# Revit family: Basin-Vanity_Sink-American_Standard-Studio_S-129700X
name_source: partatom
category: Plumbing Fixtures
units: mm (PartAtom-declared; Revit-internal decimal feet)

## family parameters
Always vertical = No
Cut with Voids When Loaded = Yes
OmniClass Number = 23.45.05.14.14
OmniClass Title = Sinks/Lavatories
Part Type = Normal
Room Calculation Point = No
Round Connector Dimension = Use Diameter
Shared = Yes
Work Plane-Based = Yes

## types (2) — shared parameters
ADA Compliant = Yes
CW Connection = Yes
CWFU = 1.5
Cold Water Connection Diameter = 1/2"
Cold Water Connection Height = 20 1/4"
Cold Water Connection Width = 4"
Default Elevation = 31"
Finish = Vitreous China-American Standard-020-White
HW Connection = Yes
HWFU = 1.5
Height = 1 5/16"
Hot Water Connection Diameter = 1/2"
Hot Water Connection Height = 20 1/4"
Hot Water Connection Width = 4"
IAPMO Compliance = ASME A112.19.2/CSA B 45.1
Installation Type = Counter
Length = 20"
Manufacturer = American Standard
Material = Vitreous China-American Standard-020-White
Price = Prices may vary. Please consult Manufacturer Representative for most up-to-date price list.
Product Documentation Link = https://americanstandard.box.com
Product Page URL = https://www.americanstandard-us.com
Revised Date = 05/03/2022
URL = http://www.americanstandard-us.com
Vent Connection = No
WFU = 2
Warranty Documentation Link = https://www.americanstandard-us.com
Waste Connection = Yes
Waste Connection Diameter = 1 1/4"
Waste Connection Height = 18 1/8"
Width = 24"

## per-type parameters (varying)
| type | Assembly Code | Description | Faucet hole Center only | Faucet hole HCW | Faucet hole HW CW |
| 1297008.020 | D2010310 | Studio® S 24-Inch Vitreous China Vanity Sink Top 8-Inch Centers | No | 1 5/16" | Yes |
| 1297001.020 | D2010300 | Studio® S 24-Inch Vitreous China Vanity Sink Top Center Hole Only | Yes | 0" | No |

note: column(s) folded — value = type name in every type: Model

## geometry (parser evidence)
native form markers: Sweep x2
no freeform markers — native parametric forms only
